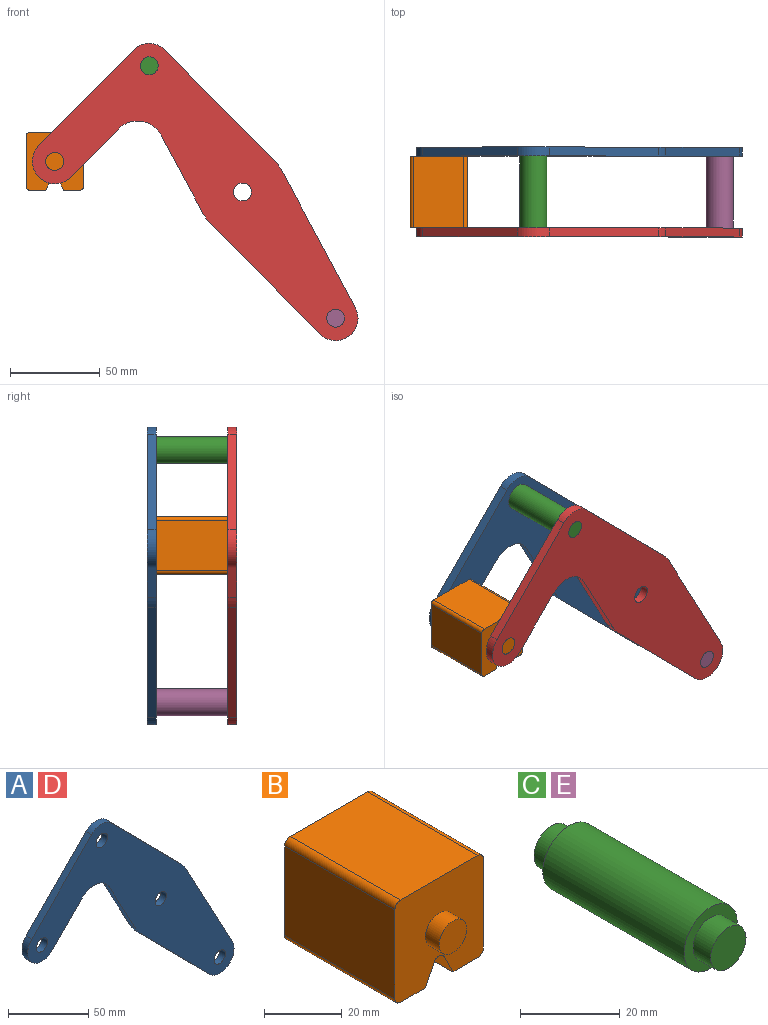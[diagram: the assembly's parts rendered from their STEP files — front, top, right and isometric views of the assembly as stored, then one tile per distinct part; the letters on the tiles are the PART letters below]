
ASSEMBLY  parts=5 mates=3
PART A: 18 faces, bbox 181.7x5x165.8 mm
  f0: plane 43.49x23.35mm, normal (-0.88,0,-0.47), area 246.8mm2, adj f1,f14,f16,f17
  f1: cylinder r=25mm len=5.75mm, axis (0,1,0), area 35.8mm2, adj f0,f2,f16,f17
  f2: plane 61.6x60.87mm, normal (-0.71,0,-0.7), area 433mm2, adj f1,f3,f16,f17
  f3: cylinder r=12.5mm len=21.39mm, axis (0,1,0), area 178.4mm2, adj f2,f4,f16,f17
  f4: plane 76.3x40.96mm, normal (0.88,0,0.47), area 433mm2, adj f3,f5,f16,f17
  f5: cylinder r=25mm len=5.75mm, axis (0,1,0), area 35.8mm2, adj f4,f6,f16,f17
  f6: plane 61.6x60.87mm, normal (0.71,0,0.7), area 433mm2, adj f5,f7,f16,f17
  f7: cylinder r=12.5mm len=17.78mm, axis (0,1,0), area 98.9mm2, adj f6,f8,f16,f17
  f8: plane 53.35x52.71mm, normal (-0.71,0,0.7), area 375mm2, adj f7,f9,f16,f17
  f9: cylinder r=12.5mm len=21.39mm, axis (0,1,0), area 196.3mm2, adj f8,f10,f16,f17
  f10: plane 26.86x26.54mm, normal (0.71,0,-0.7), area 188.8mm2, adj f9,f14,f16,f17
  f11: cylinder r=5mm len=10mm, axis (0,1,0), area 157.1mm2, adj f16,f17
  f12: cylinder r=5mm len=10mm, axis (0,1,0), area 157.1mm2, adj f16,f17
  f13: cylinder r=5mm len=10mm, axis (0,1,0), area 157.1mm2, adj f16,f17
  f14: cylinder r=15mm len=23.89mm, axis (0,1,0), area 140.2mm2, adj f0,f10,f16,f17
  f15: cylinder r=5mm len=10mm, axis (0,1,0), area 157.1mm2, adj f16,f17
  f16: plane 181.66x165.78mm, normal (0,-1,0), area 8710.1mm2, adj f0,f1,f2,f3,f4,f5,f6,f7
  f17: plane 181.66x165.78mm, normal (0,1,0), area 8710.1mm2, adj f0,f1,f2,f3,f4,f5,f6,f7
PART B: 18 faces, bbox 32.1x50x32.1 mm
  f0: plane 40x28.08mm, normal (1,0,0), area 1123.1mm2, adj f4,f10,f13,f14
  f1: plane 40x9.04mm, normal (0,0,-1), area 361.6mm2, adj f2,f4,f10,f14
  f2: plane 40x6.42mm, normal (-0.89,0,-0.45), area 287.2mm2, adj f1,f4,f10,f15
  f3: plane 40x6.42mm, normal (0.89,0,-0.45), area 287.2mm2, adj f4,f5,f10,f15
  f4: plane 32.08x32.08mm, normal (0,-1,0), area 900.6mm2, adj f0,f1,f2,f3,f5,f6,f7,f9
  f5: plane 40x9.04mm, normal (0,0,-1), area 361.6mm2, adj f3,f4,f10,f16
  f6: plane 40x28.08mm, normal (0,0,1), area 1123.1mm2, adj f4,f10,f13,f17
  f7: plane 40x28.08mm, normal (-1,0,0), area 1123.1mm2, adj f4,f10,f16,f17
  f8: plane 10x10mm, normal (0,-1,0), area 78.5mm2, adj f9
  f9: cylinder r=5mm len=10mm, axis (0,1,0), area 157.1mm2, adj f4,f8
  f10: plane 32.08x32.08mm, normal (0,1,0), area 900.6mm2, adj f0,f1,f2,f3,f5,f6,f7,f12
  f11: plane 10x10mm, normal (0,1,0), area 78.5mm2, adj f12
  f12: cylinder r=5mm len=10mm, axis (0,-1,0), area 157.1mm2, adj f10,f11
  f13: cylinder r=2mm len=40mm, axis (0,1,0), area 125.7mm2, adj f0,f4,f6,f10
  f14: cylinder r=2mm len=40mm, axis (0,-1,0), area 125.7mm2, adj f0,f1,f4,f10
  f15: cylinder r=2mm len=40mm, axis (0,1,0), area 177.1mm2, adj f2,f3,f4,f10
  f16: cylinder r=2mm len=40mm, axis (0,1,0), area 125.7mm2, adj f4,f5,f7,f10
  f17: cylinder r=2mm len=40mm, axis (0,-1,0), area 125.7mm2, adj f4,f6,f7,f10
PART C: 7 faces, bbox 15x50x15 mm
  f0: cylinder r=7.5mm len=40mm, axis (0,-1,0), area 1885mm2, adj f2,f5
  f1: cylinder r=5mm len=10mm, axis (0,1,0), area 157.1mm2, adj f2,f3
  f2: plane 15x15mm, normal (0,-1,0), area 98.2mm2, adj f0,f1
  f3: plane 10x10mm, normal (0,-1,0), area 78.5mm2, adj f1
  f4: cylinder r=5mm len=10mm, axis (0,-1,0), area 157.1mm2, adj f5,f6
  f5: plane 15x15mm, normal (0,1,0), area 98.2mm2, adj f0,f4
  f6: plane 10x10mm, normal (0,1,0), area 78.5mm2, adj f4
PART D: same geometry as A
PART E: same geometry as C
PLACE A t=(0,25,0)mm
PLACE B t=(0,-20,0)mm
PLACE C t=(0,-20,0)mm
PLACE D t=(0,-20,0)mm fixed
PLACE E t=(103.95,-20,-140.78)mm
MATE fastened E.f0 <-> D.f3  axis (0,1,0) through (51.98,-20,-70.39)mm
MATE fastened A.f7 <-> C.f0  axis (0,-1,0) through (-51.98,20,70.39)mm
MATE revolute D.f9 <-> B.f9  axis (0,1,0) through (-104.69,-20,17.04)mm
